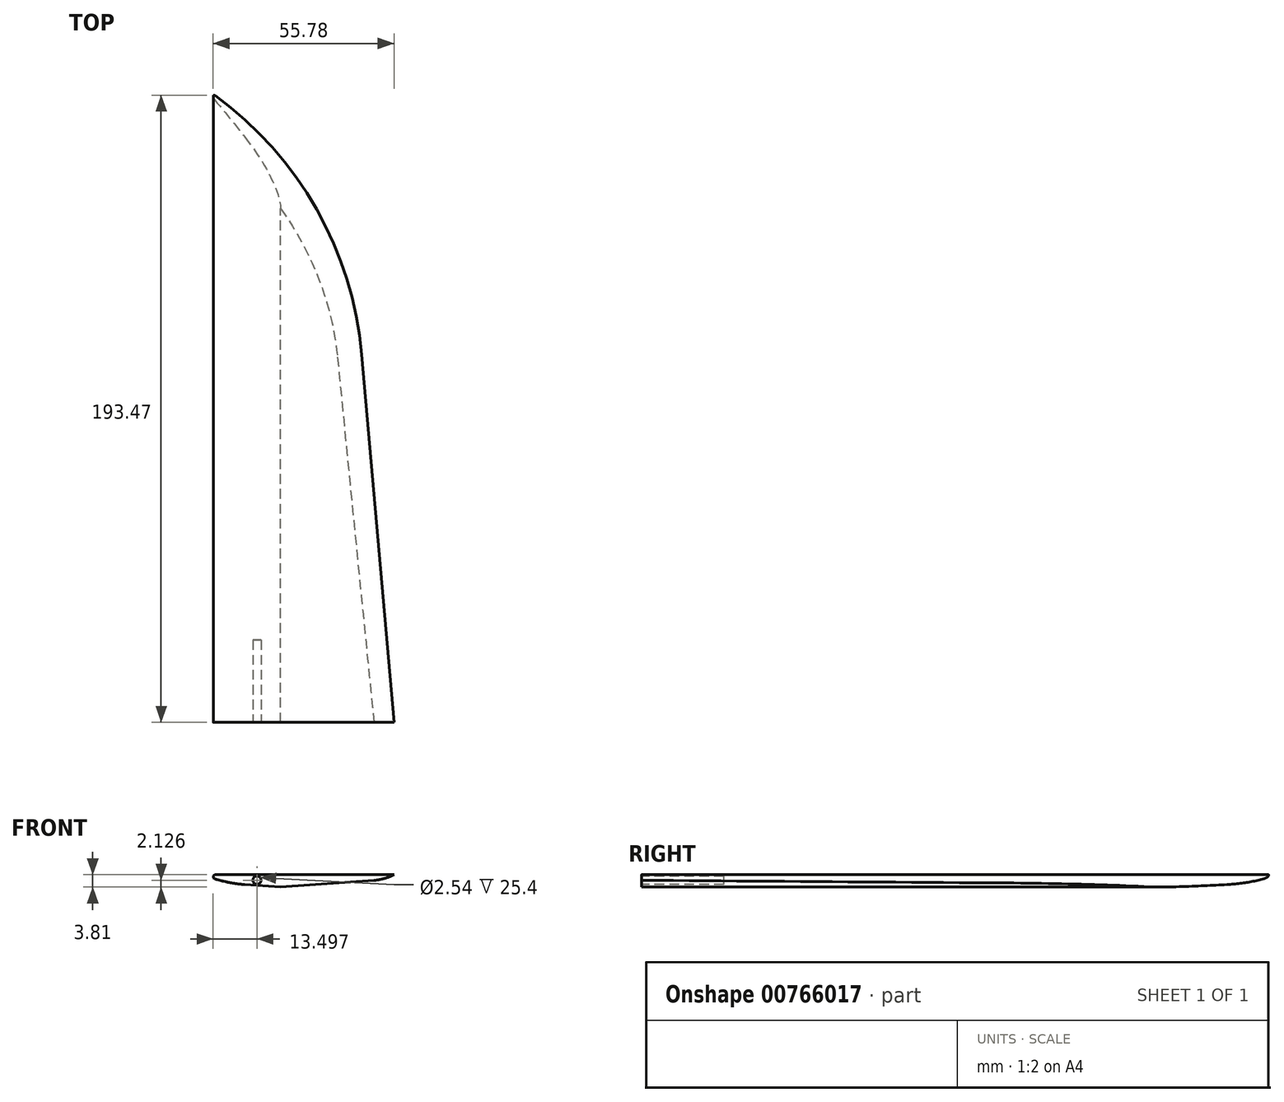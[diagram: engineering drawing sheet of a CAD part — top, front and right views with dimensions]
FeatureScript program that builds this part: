
annotation { "Feature Type Name" : "Feature", "Feature Type Description" : "" }
export const myFeature = defineFeature(function(context is Context, id is Id, definition is map)
    precondition{}
    {
        {
            var Q0;
            Q0=qCreatedBy(makeId("Front.planeOp"),FACE);
            var sketch = newSketch(context, id + "F0", { "sketchPlane" : qUnion([Q0])});
            skLineSegment(sketch, "E0", {"start": v(-21.8, 0) * mm, "end": v(-13.72, 0) * mm});
            skLineSegment(sketch, "E1", {"start": v(-13.72, 0) * mm, "end": v(55.2, 0) * mm});
            skLineSegment(sketch, "E2", {"start": v(54.4, 0) * mm, "end": v(55.2, 0) * mm});
            skLineSegment(sketch, "E3", {"start": v(54.4, 0) * mm, "end": v(1.87, -3.81) * mm});
            skLineSegment(sketch, "E4", {"start": v(-15.54, -2.58) * mm, "end": v(-21.8, 0) * mm});
            skLineSegment(sketch, "E5", {"start": v(-15.54, -2.58) * mm, "end": v(1.87, -3.81) * mm});
            skSolve(sketch);
        }
        {
            var Q0;
            Q0=makeQuery(id+"F0.imprint","IMPRINT",FACE,{"disambiguationData":[TD([[makeQuery(id+"F0.imprint","IMPRINT",EDGE,{"derivedFrom":sQuery(id+"F0.wireOp",EDGE,"E0")}),-1.0]])]});
            extrude(context, id + "F1", {"entities" : qUnion([Q0]), "endBound" : BoundingType.SYMMETRIC, "depth" : 203.2 * mm});
        }
        {
            var Q0;
            Q0=makeQuery(id+"F1.opExtrude","SWEPT_EDGE",EDGE,{"disambiguationData":[OSD([sQuery(id+"F0.wireOp",EDGE,"E4"),sQuery(id+"F0.wireOp",EDGE,"E5")])]});
            fillet(context, id + "F2", {"entities" : qUnion([Q0]), "radius" : 39.3 * mm, "tangentPropagation" : true, "allowEdgeOverflow" : false});
        }
        {
            var Q0;
            Q0=makeQuery(id+"F2.opFillet","BLEND_EDGE",EDGE,{"blendedFrom":[makeQuery(id+"F1.opExtrude","CAP_EDGE",EDGE,{"disambiguationData":[OSD([sQuery(id+"F0.wireOp",EDGE,"E0"),sQuery(id+"F0.wireOp",EDGE,"E1")])],"isStart":true}),makeQuery(id+"F1.opExtrude","SWEPT_FACE",FACE,{"disambiguationData":[OSD([sQuery(id+"F0.wireOp",EDGE,"Yl80cvIa-2GbM-w881-rLNI-stYDHtyWlVnb")])]})],"blendedInto":[makeQuery(id+"F1.opExtrude","SWEPT_FACE",FACE,{"disambiguationData":[OSD([sQuery(id+"F0.wireOp",EDGE,"Yl80cvIa-2GbM-w881-rLNI-stYDHtyWlVnb")])]})]});
            var Q1;
            Q1=makeQuery(id+"F1.opExtrude","CAP_EDGE",EDGE,{"disambiguationData":[OSD([sQuery(id+"F0.wireOp",EDGE,"E0"),sQuery(id+"F0.wireOp",EDGE,"E1")])],"isStart":true});
            fillet(context, id + "F3", {"entities" : qUnion([Q0, Q1]), "radius" : 13.97 * mm, "tangentPropagation" : true, "allowEdgeOverflow" : false});
        }
        {
            var Q0;
            Q0=makeQuery(id+"F3.opFillet","BLEND_EDGE",EDGE,{"blendedFrom":[makeQuery(id+"F1.opExtrude","CAP_EDGE",EDGE,{"disambiguationData":[OSD([sQuery(id+"F0.wireOp",EDGE,"E0"),sQuery(id+"F0.wireOp",EDGE,"E1")])],"isStart":true}),makeQuery(id+"F1.opExtrude","SWEPT_FACE",FACE,{"disambiguationData":[OSD([sQuery(id+"F0.wireOp",EDGE,"E3")])]})],"blendedInto":[makeQuery(id+"F1.opExtrude","SWEPT_FACE",FACE,{"disambiguationData":[OSD([sQuery(id+"F0.wireOp",EDGE,"E3")])]})]});
            var Q1;
            Q1=makeQuery(id+"F3.opFillet","BLEND_EDGE",EDGE,{"blendedFrom":[makeQuery(id+"F1.opExtrude","CAP_EDGE",EDGE,{"disambiguationData":[OSD([sQuery(id+"F0.wireOp",EDGE,"E0"),sQuery(id+"F0.wireOp",EDGE,"E1")])],"isStart":true}),makeQuery(id+"F1.opExtrude","SWEPT_FACE",FACE,{"disambiguationData":[OSD([sQuery(id+"F0.wireOp",EDGE,"E5")])]})],"blendedInto":[makeQuery(id+"F1.opExtrude","SWEPT_FACE",FACE,{"disambiguationData":[OSD([sQuery(id+"F0.wireOp",EDGE,"E5")])]})]});
            var Q2;
            Q2=makeQuery(id+"F3.opFillet","BLEND_EDGE",EDGE,{"blendedFrom":[makeQuery(id+"F1.opExtrude","CAP_EDGE",EDGE,{"disambiguationData":[OSD([sQuery(id+"F0.wireOp",EDGE,"E0"),sQuery(id+"F0.wireOp",EDGE,"E1")])],"isStart":true}),makeQuery(id+"F1.opExtrude","SWEPT_FACE",FACE,{"disambiguationData":[OSD([sQuery(id+"F0.wireOp",EDGE,"E4")])]})],"blendedInto":[makeQuery(id+"F1.opExtrude","SWEPT_FACE",FACE,{"disambiguationData":[OSD([sQuery(id+"F0.wireOp",EDGE,"E4")])]})]});
            fillet(context, id + "F4", {"entities" : qUnion([Q0, Q1, Q2]), "radius" : 0.64 * mm, "tangentPropagation" : true, "allowEdgeOverflow" : false});
        }
        {
            var Q0;
            Q0=makeQuery(id+"F1.opExtrude","CAP_FACE",FACE,{"disambiguationData":[OSD([sQuery(id+"F0.wireOp",EDGE,"E0"),sQuery(id+"F0.wireOp",EDGE,"E1"),sQuery(id+"F0.wireOp",EDGE,"E3"),sQuery(id+"F0.wireOp",EDGE,"Yl80cvIa-2GbM-w881-rLNI-stYDHtyWlVnb"),sQuery(id+"F0.wireOp",EDGE,"E4")])],"isStart":false});
            var sketch = newSketch(context, id + "F5", { "sketchPlane" : qUnion([Q0])});
            skCircle(sketch, "E6", {"center": v(-5.41, -1.68) * mm, "radius": 1.27 * mm});
            skSolve(sketch);
        }
        {
            var Q0;
            Q0=makeQuery(id+"F1.opExtrude","SWEPT_FACE",FACE,{"disambiguationData":[OSD([sQuery(id+"F0.wireOp",EDGE,"E0"),sQuery(id+"F0.wireOp",EDGE,"E1")])]});
            var sketch = newSketch(context, id + "F6", { "sketchPlane" : qUnion([Q0])});
            skLineSegment(sketch, "E7.bottom", {"start": v(-20.62, -101.6) * mm, "end": v(40, -101.6) * mm});
            skLineSegment(sketch, "E7.top", {"start": v(-20.62, 102.79) * mm, "end": v(40, 102.79) * mm});
            skLineSegment(sketch, "E7.left", {"start": v(-20.62, -101.6) * mm, "end": v(-20.62, 102.79) * mm});
            skLineSegment(sketch, "E7.right", {"start": v(40, -101.6) * mm, "end": v(40, 102.79) * mm});
            skLineSegment(sketch, "E8", {"start": v(-20.62, 102.79) * mm, "end": v(-20.62, 93.65) * mm});
            skLineSegment(sketch, "E9", {"start": v(-20.62, 93.65) * mm, "end": v(22.01, 68.12) * mm});
            skLineSegment(sketch, "E10", {"start": v(22.01, 68.12) * mm, "end": v(36.87, -101.6) * mm});
            skLineSegment(sketch, "E11", {"start": v(36.87, -101.6) * mm, "end": v(40, -101.6) * mm});
            skLineSegment(sketch, "E12", {"start": v(40, 102.79) * mm, "end": v(-20.62, 102.79) * mm});
            skSolve(sketch);
        }
        {
            var Q0;
            {var subQ4=sQuery(id+"F6.wireOp",EDGE,"E10");Q0=makeQuery(id+"F6.imprint","IMPRINT",FACE,{"disambiguationData":[TD([[makeQuery(id+"F6.imprint","IMPRINT",EDGE,{"derivedFrom":subQ4}),1.0]])]});}
            var Q1;
            Q1=makeQuery(id+"F6.imprint","IMPRINT",FACE,{"disambiguationData":[TD([[makeQuery(id+"F6.imprint","IMPRINT",EDGE,{"derivedFrom":sQuery(id+"F6.wireOp",EDGE,"E7.right")}),1.0]])]});
            extrude(context, id + "F7", {"entities" : qUnion([Q0, Q1]), "operationType" : NewBodyOperationType.REMOVE, "oppositeDirection" : true, "depth" : 25.4 * mm, "offsetDistance" : 25.4 * mm});
        }
        {
            var Q0;
            Q0=makeQuery(id+"F7.boolean.opBoolean","COPY",EDGE,{"derivedFrom":makeQuery(id+"F7.opExtrude","SWEPT_EDGE",EDGE,{"disambiguationData":[OSD([sQuery(id+"F6.wireOp",EDGE,"E9"),sQuery(id+"F6.wireOp",EDGE,"E10")])]})});
            fillet(context, id + "F8", {"entities" : qUnion([Q0]), "radius" : 110.64 * mm, "tangentPropagation" : true, "allowEdgeOverflow" : false});
        }
        {
            var Q0;
            Q0=makeQuery(id+"F7.boolean.opBoolean","INTERSECT",EDGE,{"derivedFrom":[makeQuery(id+"F1.opExtrude","SWEPT_FACE",FACE,{"disambiguationData":[OSD([sQuery(id+"F0.wireOp",EDGE,"E3")])]}),makeQuery(id+"F7.opExtrude","SWEPT_FACE",FACE,{"disambiguationData":[OSD([sQuery(id+"F6.wireOp",EDGE,"E10")])]})]});
            fillet(context, id + "F9", {"entities" : qUnion([Q0]), "radius" : 15.97 * mm, "tangentPropagation" : true, "allowEdgeOverflow" : false});
        }
        {
            var Q0;
            Q0=makeQuery(id+"F5.imprint","IMPRINT",FACE,{"disambiguationData":[TD([[makeQuery(id+"F5.imprint","IMPRINT",EDGE,{"derivedFrom":sQuery(id+"F5.wireOp",EDGE,"E6")}),1.0]])]});
            extrude(context, id + "F10", {"entities" : qUnion([Q0]), "operationType" : NewBodyOperationType.REMOVE, "oppositeDirection" : true, "depth" : 25.4 * mm, "offsetDistance" : 25.4 * mm});
        }
    });
